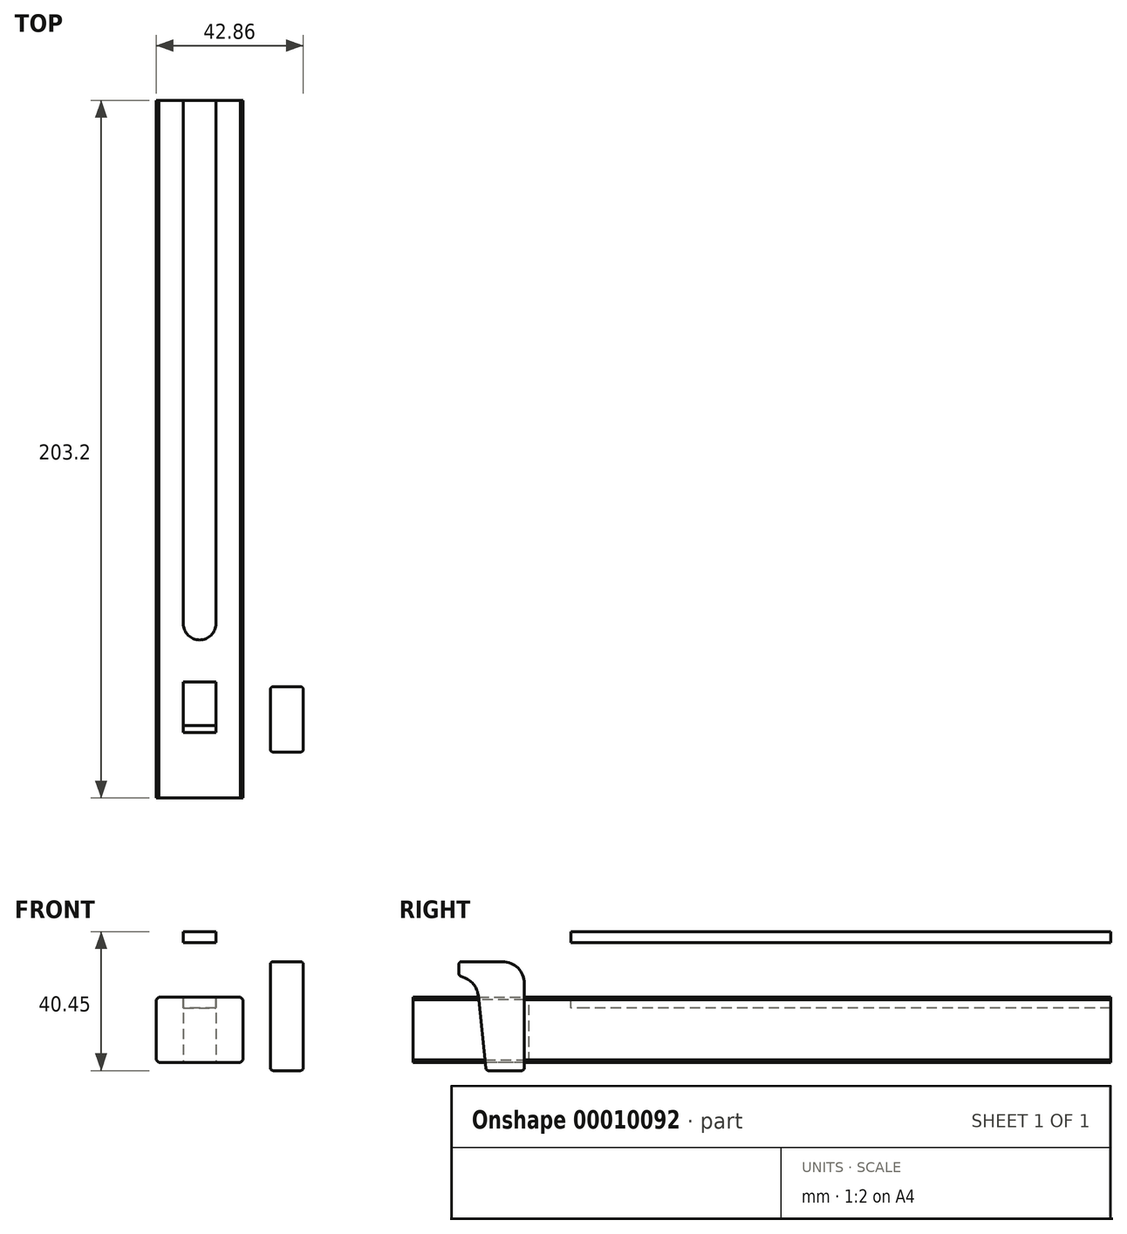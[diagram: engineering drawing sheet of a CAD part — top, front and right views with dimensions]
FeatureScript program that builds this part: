
annotation { "Feature Type Name" : "Feature", "Feature Type Description" : "" }
export const myFeature = defineFeature(function(context is Context, id is Id, definition is map)
    precondition{}
    {
        {
            var Q0;
            Q0=qCreatedBy(makeId("Front.planeOp"),FACE);
            var sketch = newSketch(context, id + "F0", { "sketchPlane" : qUnion([Q0])});
            skLineSegment(sketch, "E0.rect.bottom", {"start": v(12.7, 9.53) * mm, "end": v(-12.7, 9.53) * mm});
            skLineSegment(sketch, "E0.rect.top", {"start": v(12.7, -9.53) * mm, "end": v(-12.7, -9.53) * mm});
            skLineSegment(sketch, "E0.rect.left", {"start": v(12.7, 9.53) * mm, "end": v(12.7, -9.53) * mm});
            skLineSegment(sketch, "E0.rect.right", {"start": v(-12.7, 9.53) * mm, "end": v(-12.7, -9.53) * mm});
            skPoint(sketch, "E0.rect.middle", {"position": v(0, 0) * mm});
            skSolve(sketch);
        }
        {
            var Q0;
            Q0=makeQuery(id+"F0.imprint","IMPRINT",FACE,{"disambiguationData":[TD([[makeQuery(id+"F0.imprint","IMPRINT",EDGE,{"derivedFrom":sQuery(id+"F0.wireOp",EDGE,"E0.rect.bottom")}),1.0]])]});
            extrude(context, id + "F1", {"entities" : qUnion([Q0]), "endBound" : BoundingType.SYMMETRIC, "depth" : 203.2 * mm});
        }
        {
            var Q0;
            Q0=makeQuery(id+"F1.opExtrude","SWEPT_EDGE",EDGE,{"disambiguationData":[OSD([sQuery(id+"F0.wireOp",EDGE,"E0.rect.bottom"),sQuery(id+"F0.wireOp",EDGE,"E0.rect.right")])]});
            var Q1;
            Q1=makeQuery(id+"F1.opExtrude","SWEPT_EDGE",EDGE,{"disambiguationData":[OSD([sQuery(id+"F0.wireOp",EDGE,"E0.rect.bottom"),sQuery(id+"F0.wireOp",EDGE,"E0.rect.left")])]});
            var Q2;
            Q2=makeQuery(id+"F1.opExtrude","SWEPT_EDGE",EDGE,{"disambiguationData":[OSD([sQuery(id+"F0.wireOp",EDGE,"E0.rect.top"),sQuery(id+"F0.wireOp",EDGE,"E0.rect.left")])]});
            var Q3;
            Q3=makeQuery(id+"F1.opExtrude","SWEPT_EDGE",EDGE,{"disambiguationData":[OSD([sQuery(id+"F0.wireOp",EDGE,"E0.rect.top"),sQuery(id+"F0.wireOp",EDGE,"E0.rect.right")])]});
            chamfer(context, id + "F2", {"entities" : qUnion([Q0, Q1, Q2, Q3]), "width" : 0.8 * mm, "tangentPropagation" : true});
        }
        {
            var Q0;
            Q0=qCreatedBy(makeId("Right.planeOp"),FACE);
            var sketch = newSketch(context, id + "F3", { "sketchPlane" : qUnion([Q0])});
            skLineSegment(sketch, "E1", {"start": v(-82.55, 9.53) * mm, "end": v(-80.55, -9.53) * mm});
            skLineSegment(sketch, "E2.0", {"start": v(-82.55, 9.53) * mm, "end": v(-67.85, 9.53) * mm});
            skLineSegment(sketch, "E3.0", {"start": v(-67.85, -9.53) * mm, "end": v(-80.55, -9.53) * mm});
            skLineSegment(sketch, "E4", {"start": v(-67.85, -9.53) * mm, "end": v(-67.85, 9.53) * mm});
            skPoint(sketch, "E5.orphan", {"position": v(-101.6, 9.53) * mm});
            skPoint(sketch, "E6.orphan", {"position": v(-101.6, -9.53) * mm});
            skPoint(sketch, "E7.orphan", {"position": v(101.6, -9.53) * mm});
            skPoint(sketch, "E8.orphan", {"position": v(101.6, 9.53) * mm});
            skSolve(sketch);
        }
        {
            var Q0;
            Q0 = qSketchRegion(id + "F3", true);
            extrude(context, id + "F4", {"entities" : qUnion([Q0]), "operationType" : NewBodyOperationType.REMOVE, "endBound" : BoundingType.SYMMETRIC, "oppositeDirection" : true, "depth" : 9.52 * mm});
        }
        {
            var Q0;
            Q0=makeQuery(id+"F1.opExtrude","SWEPT_FACE",FACE,{"disambiguationData":[OSD([sQuery(id+"F0.wireOp",EDGE,"E0.rect.bottom")])]});
            var sketch = newSketch(context, id + "F5", { "sketchPlane" : qUnion([Q0])});
            skLineSegment(sketch, "E9", {"start": v(0, 101.6) * mm, "end": v(0, -67.85) * mm, "construction": true});
            skLineSegment(sketch, "E10.bottom", {"start": v(4.76, 101.6) * mm, "end": v(-4.76, 101.6) * mm});
            skLineSegment(sketch, "E10.top", {"start": v(4.76, -50.8) * mm, "end": v(-4.76, -50.8) * mm});
            skLineSegment(sketch, "E10.left", {"start": v(4.76, 101.6) * mm, "end": v(4.76, -50.8) * mm});
            skLineSegment(sketch, "E10.right", {"start": v(-4.76, 101.6) * mm, "end": v(-4.76, -50.8) * mm});
            skCircle(sketch, "E11", {"center": v(0, -50.8) * mm, "radius": 4.76 * mm});
            skSolve(sketch);
        }
        {
            var Q0;
            Q0 = qSketchRegion(id + "F5", true);
            extrude(context, id + "F6", {"entities" : qUnion([Q0]), "operationType" : NewBodyOperationType.REMOVE, "oppositeDirection" : true, "depth" : 3.17 * mm});
        }
        {
            var Q0;
            Q0=qCreatedBy(makeId("Top.planeOp"),FACE);
            cPlane(context, id + "F7", {"entities" : qUnion([Q0]), "cplaneType" : CPlaneType.OFFSET, "offset" : 25.4 * mm, "width" : 152.4 * mm, "height" : 152.4 * mm});
        }
        {
            var Q0;
            Q0=qCreatedBy(id+"F7.planeOp",FACE);
            var sketch = newSketch(context, id + "F8", { "sketchPlane" : qUnion([Q0])});
            skLineSegment(sketch, "E12.0.0", {"start": v(4.76, -50.8) * mm, "end": v(4.76, 101.6) * mm});
            skLineSegment(sketch, "E12.0.1", {"start": v(4.76, 101.6) * mm, "end": v(-4.76, 101.6) * mm});
            skLineSegment(sketch, "E12.0.2", {"start": v(-4.76, 101.6) * mm, "end": v(-4.76, -50.8) * mm});
            skArc(sketch, "E12.0.3", {"start": v(-4.76, -50.8) * mm, "mid": v(0, -55.56) * mm, "end": v(4.76, -50.8) * mm});
            skSolve(sketch);
        }
        {
            var Q0;
            Q0 = qSketchRegion(id + "F8", true);
            extrude(context, id + "F9", {"entities" : qUnion([Q0]), "depth" : 3.17 * mm});
        }
        {
            var Q0;
            Q0=qCreatedBy(makeId("Right.planeOp"),FACE);
            cPlane(context, id + "F10", {"entities" : qUnion([Q0]), "cplaneType" : CPlaneType.OFFSET, "offset" : 25.4 * mm, "width" : 152.4 * mm, "height" : 152.4 * mm});
        }
        {
            var Q0;
            Q0=qCreatedBy(id+"F10.planeOp",FACE);
            var sketch = newSketch(context, id + "F11", { "sketchPlane" : qUnion([Q0])});
            skLineSegment(sketch, "E13.0", {"start": v(-82.55, 9.53) * mm, "end": v(-80.55, -9.53) * mm});
            skLineSegment(sketch, "E13.1", {"start": v(-67.85, -9.53) * mm, "end": v(-67.85, 9.53) * mm});
            skLineSegment(sketch, "E14", {"start": v(-82.55, 9.53) * mm, "end": v(-82.6, 9.92) * mm});
            skLineSegment(sketch, "E15", {"start": v(-80.55, -9.53) * mm, "end": v(-80.3, -11.88) * mm});
            skLineSegment(sketch, "E16", {"start": v(-80.3, -11.88) * mm, "end": v(-69.19, -11.88) * mm});
            skLineSegment(sketch, "E17", {"start": v(-69.19, -11.88) * mm, "end": v(-69.19, 13.52) * mm});
            skLineSegment(sketch, "E18", {"start": v(-75.54, 19.87) * mm, "end": v(-88.24, 19.87) * mm});
            skLineSegment(sketch, "E19", {"start": v(-88.24, 19.87) * mm, "end": v(-88.24, 15.87) * mm});
            skLineSegment(sketch, "E20", {"start": v(-88.24, 15.87) * mm, "end": v(-86.43, 15.1) * mm});
            skPoint(sketch, "E21.visualSharp", {"position": v(-69.19, 19.87) * mm});
            skArc(sketch, "E21.filletArc", {"start": v(-69.19, 13.52) * mm, "mid": v(-71.05, 18) * mm, "end": v(-75.54, 19.87) * mm});
            skPoint(sketch, "E22.visualSharp", {"position": v(-82.98, 13.64) * mm});
            skArc(sketch, "E22.filletArc", {"start": v(-82.6, 9.92) * mm, "mid": v(-83.8, 13.03) * mm, "end": v(-86.43, 15.1) * mm});
            skSolve(sketch);
        }
        {
            var Q0;
            Q0 = qSketchRegion(id + "F11", true);
            extrude(context, id + "F12", {"entities" : qUnion([Q0]), "endBound" : BoundingType.SYMMETRIC, "depth" : 9.52 * mm});
        }
        {
            var Q0;
            Q0=makeQuery(id+"F12.opExtrude","SWEPT_FACE",FACE,{"disambiguationData":[OSD([sQuery(id+"F11.wireOp",EDGE,"E13.0"),sQuery(id+"F11.wireOp",EDGE,"E14"),sQuery(id+"F11.wireOp",EDGE,"E15")])]});
            var Q1;
            Q1=makeQuery(id+"F12.opExtrude","SWEPT_FACE",FACE,{"disambiguationData":[OSD([sQuery(id+"F11.wireOp",EDGE,"E22.filletArc")])]});
            var Q2;
            Q2=makeQuery(id+"F12.opExtrude","SWEPT_FACE",FACE,{"disambiguationData":[OSD([sQuery(id+"F11.wireOp",EDGE,"E19")])]});
            var Q3;
            Q3=makeQuery(id+"F12.opExtrude","SWEPT_FACE",FACE,{"disambiguationData":[OSD([sQuery(id+"F11.wireOp",EDGE,"E20")])]});
            var Q4;
            Q4=makeQuery(id+"F12.opExtrude","SWEPT_FACE",FACE,{"disambiguationData":[OSD([sQuery(id+"F11.wireOp",EDGE,"E16")])]});
            var Q5;
            Q5=makeQuery(id+"F12.opExtrude","SWEPT_FACE",FACE,{"disambiguationData":[OSD([sQuery(id+"F11.wireOp",EDGE,"E17")])]});
            fillet(context, id + "F13", {"entities" : qUnion([Q0, Q1, Q2, Q3, Q4, Q5]), "radius" : 0.8 * mm, "tangentPropagation" : true, "allowEdgeOverflow" : false});
        }
    });
